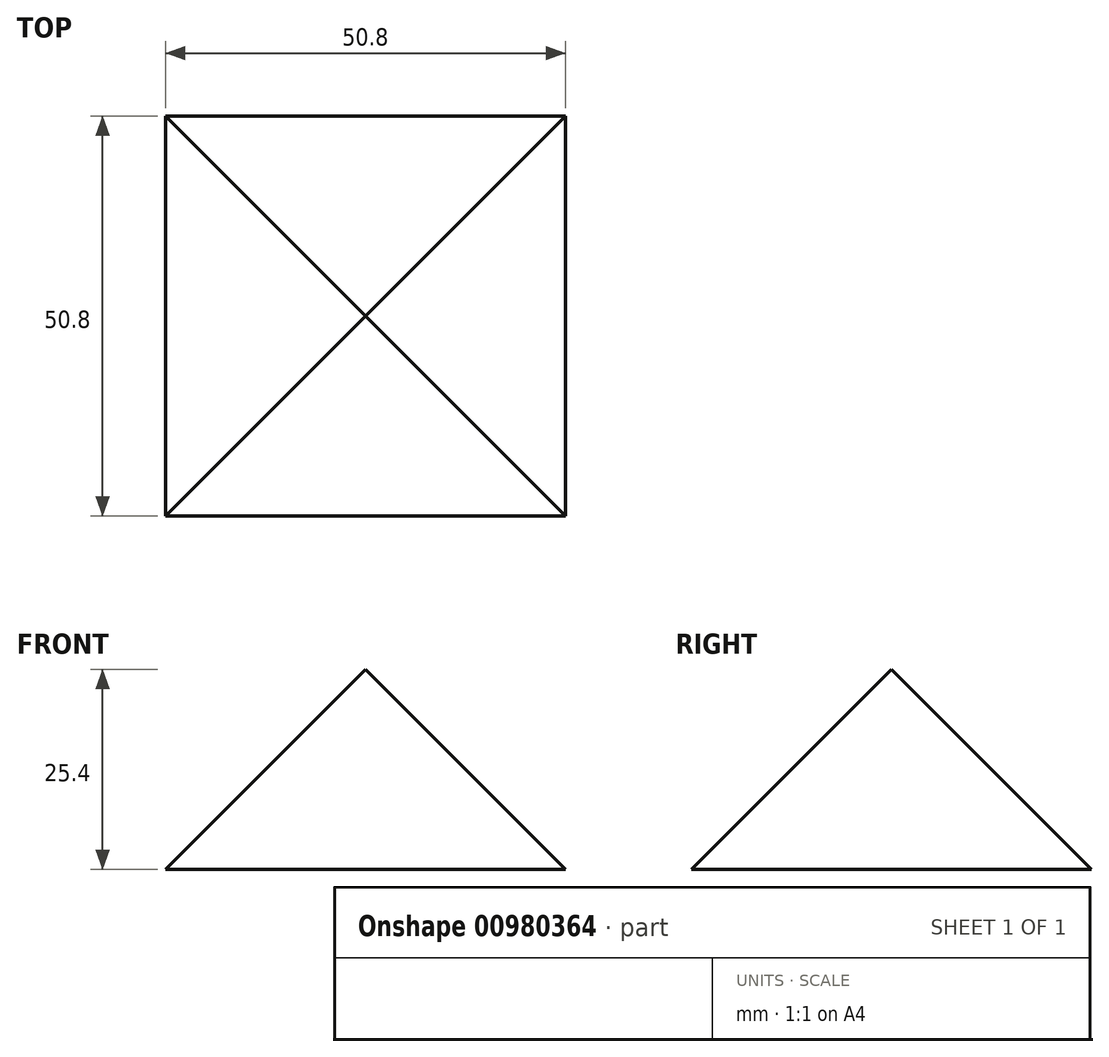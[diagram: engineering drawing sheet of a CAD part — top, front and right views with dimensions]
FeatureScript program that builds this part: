
annotation { "Feature Type Name" : "Feature", "Feature Type Description" : "" }
export const myFeature = defineFeature(function(context is Context, id is Id, definition is map)
    precondition{}
    {
        {
            var Q0;
            Q0=qCreatedBy(makeId("Top.planeOp"),FACE);
            var sketch = newSketch(context, id + "F0", { "sketchPlane" : qUnion([Q0])});
            skCircle(sketch, "E0.cCircle", {"center": v(0, 0) * mm, "radius": 25.4 * mm, "construction": true});
            skLineSegment(sketch, "E0.0", {"start": v(-25.4, 25.4) * mm, "end": v(25.4, 25.4) * mm});
            skLineSegment(sketch, "E0.1", {"start": v(25.4, 25.4) * mm, "end": v(25.4, -25.4) * mm});
            skLineSegment(sketch, "E0.2", {"start": v(25.4, -25.4) * mm, "end": v(-25.4, -25.4) * mm});
            skLineSegment(sketch, "E0.3", {"start": v(-25.4, -25.4) * mm, "end": v(-25.4, 25.4) * mm});
            skPoint(sketch, "E0.0.midPoint", {"position": v(0, 25.4) * mm});
            skSolve(sketch);
        }
        {
            var Q0;
            Q0=qCreatedBy(makeId("Top.planeOp"),FACE);
            cPlane(context, id + "F1", {"entities" : qUnion([Q0]), "cplaneType" : CPlaneType.OFFSET, "offset" : 25.4 * mm, "width" : 152.4 * mm, "height" : 152.4 * mm});
        }
        {
            var Q0;
            Q0=qCreatedBy(id+"F1.planeOp",FACE);
            var sketch = newSketch(context, id + "F2", { "sketchPlane" : qUnion([Q0])});
            skPoint(sketch, "E1", {"position": v(0, 0) * mm});
            skSolve(sketch);
        }
        {
            var Q0;
            Q0=makeQuery(id+"F0.imprint","IMPRINT",FACE,{"disambiguationData":[TD([[makeQuery(id+"F0.imprint","IMPRINT",EDGE,{"derivedFrom":sQuery(id+"F0.wireOp",EDGE,"E0.0")}),-1.0]])]});
            var Q1;
            Q1=sQuery(id+"F2.wireOp",VERTEX,"E1");
            loft(context, id + "F3", {"sheetProfilesArray" : [{ "sheetProfileEntities" : qUnion([Q0]) }, { "sheetProfileEntities" : qUnion([Q1]) }]});
        }
    });
